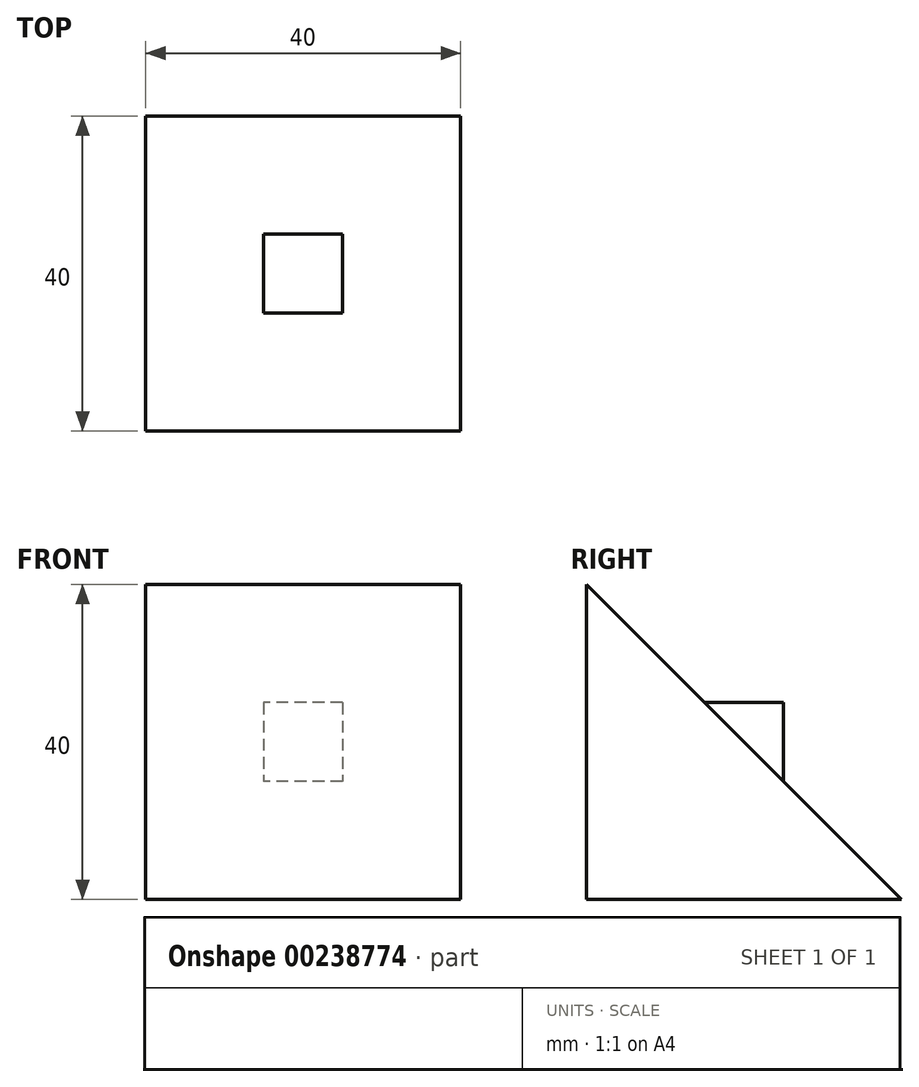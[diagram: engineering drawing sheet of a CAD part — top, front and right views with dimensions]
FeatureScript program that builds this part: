
annotation { "Feature Type Name" : "Feature", "Feature Type Description" : "" }
export const myFeature = defineFeature(function(context is Context, id is Id, definition is map)
    precondition{}
    {
        {
            var Q0;
            Q0=qCreatedBy(makeId("Right.planeOp"),FACE);
            var sketch = newSketch(context, id + "F0", { "sketchPlane" : qUnion([Q0])});
            skLineSegment(sketch, "E0.bottom", {"start": v(20, 20) * mm, "end": v(-20, 20) * mm});
            skLineSegment(sketch, "E0.top", {"start": v(20, -20) * mm, "end": v(-20, -20) * mm});
            skLineSegment(sketch, "E0.left", {"start": v(20, 20) * mm, "end": v(20, -20) * mm});
            skLineSegment(sketch, "E0.right", {"start": v(-20, 20) * mm, "end": v(-20, -20) * mm});
            skPoint(sketch, "E0.middle", {"position": v(0, 0) * mm});
            skLineSegment(sketch, "E1", {"start": v(-20, 20) * mm, "end": v(20, -20) * mm});
            skLineSegment(sketch, "E2.bottom", {"start": v(5, 5) * mm, "end": v(-5, 5) * mm});
            skLineSegment(sketch, "E2.top", {"start": v(5, -5) * mm, "end": v(-5, -5) * mm});
            skLineSegment(sketch, "E2.left", {"start": v(5, 5) * mm, "end": v(5, -5) * mm});
            skLineSegment(sketch, "E2.right", {"start": v(-5, 5) * mm, "end": v(-5, -5) * mm});
            skSolve(sketch);
        }
        {
            var Q0;
            {var subQ1=sQuery(id+"F0.wireOp",EDGE,"E0.top");Q0=makeQuery(id+"F0.imprint","IMPRINT",FACE,{"disambiguationData":[TD([[makeQuery(id+"F0.imprint","IMPRINT",EDGE,{"derivedFrom":subQ1}),-1.0]])]});}
            var Q1;
            {var subQ2=sQuery(id+"F0.wireOp",EDGE,"E2.top");Q1=makeQuery(id+"F0.imprint","IMPRINT",FACE,{"disambiguationData":[TD([[makeQuery(id+"F0.imprint","IMPRINT",EDGE,{"derivedFrom":subQ2}),-1.0]])]});}
            extrude(context, id + "F1", {"entities" : qUnion([Q0, Q1]), "endBound" : BoundingType.SYMMETRIC, "depth" : 40 * mm});
        }
        {
            var Q0;
            {var subQ0=sQuery(id+"F0.wireOp",EDGE,"E2.bottom");Q0=makeQuery(id+"F0.imprint","IMPRINT",FACE,{"disambiguationData":[TD([[makeQuery(id+"F0.imprint","IMPRINT",EDGE,{"derivedFrom":subQ0}),1.0]])]});}
            extrude(context, id + "F2", {"entities" : qUnion([Q0]), "operationType" : NewBodyOperationType.ADD, "endBound" : BoundingType.SYMMETRIC, "depth" : 10 * mm});
        }
    });
